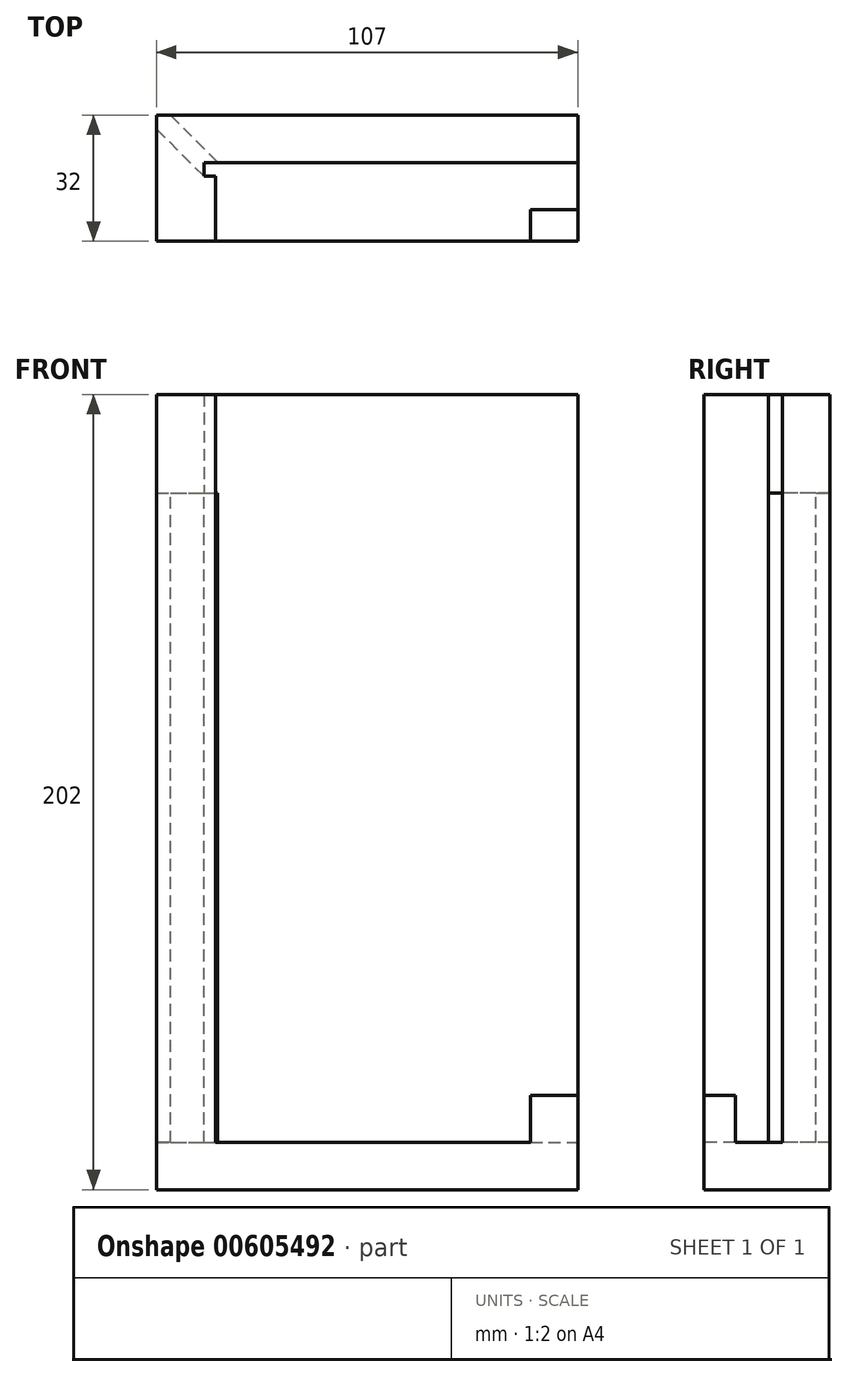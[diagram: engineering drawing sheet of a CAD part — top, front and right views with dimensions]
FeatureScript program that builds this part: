
annotation { "Feature Type Name" : "Feature", "Feature Type Description" : "" }
export const myFeature = defineFeature(function(context is Context, id is Id, definition is map)
    precondition{}
    {
        {
            var Q0;
            Q0=qCreatedBy(makeId("Top.planeOp"),FACE);
            var sketch = newSketch(context, id + "F0", { "sketchPlane" : qUnion([Q0])});
            skLineSegment(sketch, "E0", {"start": v(-28.32, 70.71) * mm, "end": v(-28.32, -10.33) * mm, "construction": true});
            skLineSegment(sketch, "E1", {"start": v(-27.64, -6.28) * mm, "end": v(-11.03, -22.9) * mm, "construction": true});
            skLineSegment(sketch, "E2", {"start": v(-15.41, -17.56) * mm, "end": v(106.8, -17.56) * mm, "construction": true});
            skLineSegment(sketch, "E3.0", {"start": v(-26.02, 70.71) * mm, "end": v(-26.02, -10.33) * mm, "construction": true});
            skLineSegment(sketch, "E4.0", {"start": v(-26.02, -4.66) * mm, "end": v(-9.4, -21.27) * mm, "construction": true});
            skLineSegment(sketch, "E5.0", {"start": v(-15.41, -15.26) * mm, "end": v(106.8, -15.26) * mm, "construction": true});
            skLineSegment(sketch, "E6.bottom", {"start": v(-15.41, -15.26) * mm, "end": v(79.59, -15.26) * mm});
            skLineSegment(sketch, "E6.top", {"start": v(-15.41, -3.26) * mm, "end": v(79.59, -3.26) * mm});
            skLineSegment(sketch, "E6.left", {"start": v(-15.41, -15.26) * mm, "end": v(-15.41, -3.26) * mm});
            skLineSegment(sketch, "E6.right", {"start": v(79.59, -15.26) * mm, "end": v(79.59, -3.26) * mm});
            skLineSegment(sketch, "E7.bottom", {"start": v(-15.41, -15.26) * mm, "end": v(-27.41, -15.26) * mm});
            skLineSegment(sketch, "E7.top", {"start": v(-15.41, -35.26) * mm, "end": v(-27.41, -35.26) * mm});
            skLineSegment(sketch, "E7.left", {"start": v(-15.41, -15.26) * mm, "end": v(-15.41, -35.26) * mm});
            skLineSegment(sketch, "E7.right", {"start": v(-27.41, -15.26) * mm, "end": v(-27.41, -35.26) * mm});
            skLineSegment(sketch, "E8.top", {"start": v(-15.41, -3.26) * mm, "end": v(-27.41, -3.26) * mm});
            skLineSegment(sketch, "E8.right", {"start": v(-27.41, -15.26) * mm, "end": v(-27.41, -3.26) * mm});
            skLineSegment(sketch, "E9", {"start": v(-27.41, -3.26) * mm, "end": v(-15.41, -15.26) * mm});
            skLineSegment(sketch, "E10.0", {"start": v(-27.79, -6.42) * mm, "end": v(-11.17, -23.04) * mm});
            skLineSegment(sketch, "E11.0", {"start": v(-23.88, -3.26) * mm, "end": v(-7.64, -19.5) * mm});
            skSolve(sketch);
        }
        {
            var Q0;
            {var subQ1=sQuery(id+"F0.wireOp",EDGE,"E6.top");Q0=makeQuery(id+"F0.imprint","IMPRINT",FACE,{"disambiguationData":[TD([[makeQuery(id+"F0.imprint","IMPRINT",EDGE,{"derivedFrom":subQ1}),-1.0]])]});}
            var Q1;
            {var subQ1=sQuery(id+"F0.wireOp",EDGE,"E8.top");var subQ3=sQuery(id+"F0.wireOp",EDGE,"E11.0");var subQ4=makeQuery(id+"F0.imprint","INTERSECT",VERTEX,{"derivedFrom":[subQ1,subQ3]});Q1=makeQuery(id+"F0.imprint","IMPRINT",FACE,{"disambiguationData":[TD([[makeQuery(id+"F0.imprint","IMPRINT",EDGE,{"disambiguationData":[TD([[subQ4,-1.0]])],"derivedFrom":subQ3}),1.0]])]});}
            var Q2;
            {var subQ0=sQuery(id+"F0.wireOp",EDGE,"E9");Q2=makeQuery(id+"F0.imprint","IMPRINT",FACE,{"disambiguationData":[TD([[makeQuery(id+"F0.imprint","IMPRINT",EDGE,{"derivedFrom":subQ0}),-1.0]])]});}
            var Q3;
            {var subQ0=sQuery(id+"F0.wireOp",EDGE,"E8.right");var subQ3=sQuery(id+"F0.wireOp",EDGE,"E10.0");var subQ5=makeQuery(id+"F0.imprint","INTERSECT",VERTEX,{"derivedFrom":[subQ0,subQ3]});Q3=makeQuery(id+"F0.imprint","IMPRINT",FACE,{"disambiguationData":[TD([[makeQuery(id+"F0.imprint","IMPRINT",EDGE,{"disambiguationData":[TD([[subQ5,-1.0]])],"derivedFrom":subQ3}),-1.0]])]});}
            var Q4;
            {var subQ6=sQuery(id+"F0.wireOp",EDGE,"E7.top");Q4=makeQuery(id+"F0.imprint","IMPRINT",FACE,{"disambiguationData":[TD([[makeQuery(id+"F0.imprint","IMPRINT",EDGE,{"derivedFrom":subQ6}),-1.0]])]});}
            var Q5;
            {var subQ0=sQuery(id+"F0.wireOp",EDGE,"E9");Q5=makeQuery(id+"F0.imprint","IMPRINT",FACE,{"disambiguationData":[TD([[makeQuery(id+"F0.imprint","IMPRINT",EDGE,{"derivedFrom":subQ0}),1.0]])]});}
            var Q6;
            {var subQ1=sQuery(id+"F0.wireOp",EDGE,"E6.bottom");var subQ3=sQuery(id+"F0.wireOp",EDGE,"E11.0");var subQ4=makeQuery(id+"F0.imprint","INTERSECT",VERTEX,{"derivedFrom":[subQ1,subQ3]});Q6=makeQuery(id+"F0.imprint","IMPRINT",FACE,{"disambiguationData":[TD([[makeQuery(id+"F0.imprint","IMPRINT",EDGE,{"disambiguationData":[TD([[subQ4,1.0]])],"derivedFrom":subQ3}),-1.0]])]});}
            var Q7;
            {var subQ1=sQuery(id+"F0.wireOp",EDGE,"E7.left");var subQ3=sQuery(id+"F0.wireOp",EDGE,"E10.0");var subQ4=makeQuery(id+"F0.imprint","INTERSECT",VERTEX,{"derivedFrom":[subQ1,subQ3]});Q7=makeQuery(id+"F0.imprint","IMPRINT",FACE,{"disambiguationData":[TD([[makeQuery(id+"F0.imprint","IMPRINT",EDGE,{"disambiguationData":[TD([[subQ4,1.0]])],"derivedFrom":subQ3}),1.0]])]});}
            extrude(context, id + "F1", {"entities" : qUnion([Q0, Q1, Q2, Q3, Q4, Q5, Q6, Q7]), "depth" : 25 * mm, "offsetDistance" : 25 * mm});
        }
        {
            var Q0;
            {var subQ6=sQuery(id+"F0.wireOp",EDGE,"E7.top");Q0=makeQuery(id+"F0.imprint","IMPRINT",FACE,{"disambiguationData":[TD([[makeQuery(id+"F0.imprint","IMPRINT",EDGE,{"derivedFrom":subQ6}),-1.0]])]});}
            var Q1;
            {var subQ1=sQuery(id+"F0.wireOp",EDGE,"E8.top");var subQ3=sQuery(id+"F0.wireOp",EDGE,"E11.0");var subQ4=makeQuery(id+"F0.imprint","INTERSECT",VERTEX,{"derivedFrom":[subQ1,subQ3]});Q1=makeQuery(id+"F0.imprint","IMPRINT",FACE,{"disambiguationData":[TD([[makeQuery(id+"F0.imprint","IMPRINT",EDGE,{"disambiguationData":[TD([[subQ4,-1.0]])],"derivedFrom":subQ3}),1.0]])]});}
            var Q2;
            {var subQ1=sQuery(id+"F0.wireOp",EDGE,"E6.top");Q2=makeQuery(id+"F0.imprint","IMPRINT",FACE,{"disambiguationData":[TD([[makeQuery(id+"F0.imprint","IMPRINT",EDGE,{"derivedFrom":subQ1}),-1.0]])]});}
            var Q3;
            {var subQ0=sQuery(id+"F0.wireOp",EDGE,"E8.right");var subQ3=sQuery(id+"F0.wireOp",EDGE,"E10.0");var subQ5=makeQuery(id+"F0.imprint","INTERSECT",VERTEX,{"derivedFrom":[subQ0,subQ3]});Q3=makeQuery(id+"F0.imprint","IMPRINT",FACE,{"disambiguationData":[TD([[makeQuery(id+"F0.imprint","IMPRINT",EDGE,{"disambiguationData":[TD([[subQ5,-1.0]])],"derivedFrom":subQ3}),-1.0]])]});}
            extrude(context, id + "F2", {"entities" : qUnion([Q0, Q1, Q2, Q3]), "operationType" : NewBodyOperationType.ADD, "oppositeDirection" : true, "depth" : 165 * mm, "offsetDistance" : 25 * mm});
        }
        {
            var Q0;
            Q0=makeQuery(id+"F2.opExtrude","CAP_FACE",FACE,{"disambiguationData":[OSD([sQuery(id+"F0.wireOp",EDGE,"E7.top"),sQuery(id+"F0.wireOp",EDGE,"E7.left"),sQuery(id+"F0.wireOp",EDGE,"E7.right"),sQuery(id+"F0.wireOp",EDGE,"E8.right"),sQuery(id+"F0.wireOp",EDGE,"E10.0")])],"isStart":false});
            var sketch = newSketch(context, id + "F3", { "sketchPlane" : qUnion([Q0])});
            skLineSegment(sketch, "E12.bottom", {"start": v(-15.41, 18.8) * mm, "end": v(-12.41, 18.8) * mm});
            skLineSegment(sketch, "E12.left", {"start": v(-15.41, 18.8) * mm, "end": v(-15.41, 30.8) * mm});
            skLineSegment(sketch, "E12.right", {"start": v(-12.41, 18.8) * mm, "end": v(-12.41, 30.8) * mm});
            skLineSegment(sketch, "E13.top", {"start": v(-12.41, 35.26) * mm, "end": v(-15.41, 35.26) * mm});
            skLineSegment(sketch, "E13.left", {"start": v(-12.41, 30.8) * mm, "end": v(-12.41, 35.26) * mm});
            skLineSegment(sketch, "E13.right", {"start": v(-15.41, 30.8) * mm, "end": v(-15.41, 35.26) * mm});
            skSolve(sketch);
        }
        {
            var Q0;
            Q0=qSketchRegion(id+"F3",true);
            var Q1;
            Q1=makeQuery(id+"F1.opExtrude","CAP_FACE",FACE,{"disambiguationData":[OSD([sQuery(id+"F0.wireOp",EDGE,"E6.bottom"),sQuery(id+"F0.wireOp",EDGE,"E6.top"),sQuery(id+"F0.wireOp",EDGE,"E6.right"),sQuery(id+"F0.wireOp",EDGE,"E7.top"),sQuery(id+"F0.wireOp",EDGE,"E7.left"),sQuery(id+"F0.wireOp",EDGE,"E7.right"),sQuery(id+"F0.wireOp",EDGE,"E8.top"),sQuery(id+"F0.wireOp",EDGE,"E8.right")])],"isStart":false});
            extrude(context, id + "F4", {"entities" : qUnion([Q0]), "operationType" : NewBodyOperationType.ADD, "endBound" : BoundingType.UP_TO_SURFACE, "oppositeDirection" : true, "depth" : 25 * mm, "endBoundEntityFace" : qUnion([Q1]), "offsetDistance" : 25 * mm});
        }
        {
            var Q0;
            Q0=makeQuery(id+"F2.opExtrude","CAP_FACE",FACE,{"disambiguationData":[OSD([sQuery(id+"F0.wireOp",EDGE,"E6.bottom"),sQuery(id+"F0.wireOp",EDGE,"E6.top"),sQuery(id+"F0.wireOp",EDGE,"E6.right"),sQuery(id+"F0.wireOp",EDGE,"E8.top"),sQuery(id+"F0.wireOp",EDGE,"E11.0")])],"isStart":false});
            var sketch = newSketch(context, id + "F5", { "sketchPlane" : qUnion([Q0])});
            skLineSegment(sketch, "E14.0.0", {"start": v(-12.41, 30.8) * mm, "end": v(-12.41, 35.26) * mm});
            skLineSegment(sketch, "E14.0.1", {"start": v(-12.41, 35.26) * mm, "end": v(-15.41, 35.26) * mm});
            skLineSegment(sketch, "E14.0.2", {"start": v(-15.41, 35.26) * mm, "end": v(-15.41, 30.8) * mm});
            skLineSegment(sketch, "E14.0.3", {"start": v(-15.41, 30.8) * mm, "end": v(-15.41, 18.8) * mm});
            skLineSegment(sketch, "E14.0.4", {"start": v(-15.41, 18.8) * mm, "end": v(-12.41, 18.8) * mm});
            skLineSegment(sketch, "E14.0.5", {"start": v(-12.41, 18.8) * mm, "end": v(-12.41, 30.8) * mm});
            skLineSegment(sketch, "E15.bottom", {"start": v(79.59, 15.26) * mm, "end": v(-12.41, 15.26) * mm});
            skLineSegment(sketch, "E15.top", {"start": v(79.59, 35.26) * mm, "end": v(-12.41, 35.26) * mm});
            skLineSegment(sketch, "E15.left", {"start": v(79.59, 15.26) * mm, "end": v(79.59, 35.26) * mm});
            skLineSegment(sketch, "E15.right", {"start": v(-12.41, 15.26) * mm, "end": v(-12.41, 35.26) * mm});
            skLineSegment(sketch, "E16.top", {"start": v(79.59, 27.26) * mm, "end": v(-12.41, 27.26) * mm});
            skLineSegment(sketch, "E16.left", {"start": v(79.59, 15.26) * mm, "end": v(79.59, 27.26) * mm});
            skLineSegment(sketch, "E16.right", {"start": v(-12.41, 15.26) * mm, "end": v(-12.41, 27.26) * mm});
            skLineSegment(sketch, "E17.bottom", {"start": v(79.59, 35.26) * mm, "end": v(67.59, 35.26) * mm});
            skLineSegment(sketch, "E17.top", {"start": v(79.59, 15.26) * mm, "end": v(67.59, 15.26) * mm});
            skLineSegment(sketch, "E17.left", {"start": v(79.59, 35.26) * mm, "end": v(79.59, 15.26) * mm});
            skLineSegment(sketch, "E17.right", {"start": v(67.59, 35.26) * mm, "end": v(67.59, 15.26) * mm});
            skSolve(sketch);
        }
        {
            var Q0;
            {var subQ0=sQuery(id+"F5.wireOp",EDGE,"E15.top");Q0=makeQuery(id+"F5.imprint","IMPRINT",FACE,{"disambiguationData":[TD([[makeQuery(id+"F5.imprint","IMPRINT",EDGE,{"derivedFrom":subQ0}),1.0]])]});}
            var Q1;
            {var subQ5=sQuery(id+"F5.wireOp",EDGE,"E17.bottom");Q1=makeQuery(id+"F5.imprint","IMPRINT",FACE,{"disambiguationData":[TD([[makeQuery(id+"F5.imprint","IMPRINT",EDGE,{"derivedFrom":subQ5}),1.0]])]});}
            var Q2;
            {var subQ5=sQuery(id+"F5.wireOp",EDGE,"E17.top");Q2=makeQuery(id+"F5.imprint","IMPRINT",FACE,{"disambiguationData":[TD([[makeQuery(id+"F5.imprint","IMPRINT",EDGE,{"derivedFrom":subQ5}),1.0]])]});}
            extrude(context, id + "F6", {"entities" : qUnion([Q0, Q1, Q2]), "operationType" : NewBodyOperationType.ADD, "oppositeDirection" : true, "depth" : 12 * mm, "offsetDistance" : 25 * mm});
        }
        {
            var Q0;
            Q0=makeQuery(id+"F6.boolean.opBoolean","MERGE",FACE,{"derivedFrom":[makeQuery(id+"F2.opExtrude","CAP_FACE",FACE,{"disambiguationData":[OSD([sQuery(id+"F0.wireOp",EDGE,"E6.bottom"),sQuery(id+"F0.wireOp",EDGE,"E6.top"),sQuery(id+"F0.wireOp",EDGE,"E6.right"),sQuery(id+"F0.wireOp",EDGE,"E8.top"),sQuery(id+"F0.wireOp",EDGE,"E11.0")])],"isStart":false}),makeQuery(id+"F4.boolean.opBoolean","MERGE",FACE,{"derivedFrom":[makeQuery(id+"F2.opExtrude","CAP_FACE",FACE,{"disambiguationData":[OSD([sQuery(id+"F0.wireOp",EDGE,"E7.top"),sQuery(id+"F0.wireOp",EDGE,"E7.left"),sQuery(id+"F0.wireOp",EDGE,"E7.right"),sQuery(id+"F0.wireOp",EDGE,"E8.right"),sQuery(id+"F0.wireOp",EDGE,"E10.0")])],"isStart":false}),makeQuery(id+"F4.opExtrude","CAP_FACE",FACE,{"disambiguationData":[OSD([sQuery(id+"F3.wireOp",EDGE,"E12.bottom"),sQuery(id+"F3.wireOp",EDGE,"E12.left"),sQuery(id+"F3.wireOp",EDGE,"E12.right"),sQuery(id+"F3.wireOp",EDGE,"E13.top"),sQuery(id+"F3.wireOp",EDGE,"E13.left"),sQuery(id+"F3.wireOp",EDGE,"E13.right")])],"isStart":true})]}),makeQuery(id+"F6.opExtrude","CAP_FACE",FACE,{"disambiguationData":[OSD([sQuery(id+"F5.wireOp",EDGE,"E15.top"),sQuery(id+"F5.wireOp",EDGE,"E15.right"),sQuery(id+"F5.wireOp",EDGE,"E16.top"),sQuery(id+"F5.wireOp",EDGE,"E17.bottom"),sQuery(id+"F5.wireOp",EDGE,"E17.top"),sQuery(id+"F5.wireOp",EDGE,"E17.left"),sQuery(id+"F5.wireOp",EDGE,"E17.right")])],"isStart":true})]});
            var sketch = newSketch(context, id + "F7", { "sketchPlane" : qUnion([Q0])});
            skLineSegment(sketch, "E18.bottom", {"start": v(79.59, 3.26) * mm, "end": v(-27.41, 3.26) * mm});
            skLineSegment(sketch, "E18.top", {"start": v(79.59, 35.26) * mm, "end": v(-27.41, 35.26) * mm});
            skLineSegment(sketch, "E18.left", {"start": v(79.59, 3.26) * mm, "end": v(79.59, 35.26) * mm});
            skLineSegment(sketch, "E18.right", {"start": v(-27.41, 3.26) * mm, "end": v(-27.41, 35.26) * mm});
            skSolve(sketch);
        }
        {
            var Q0;
            Q0 = qSketchRegion(id + "F7", true);
            extrude(context, id + "F8", {"entities" : qUnion([Q0]), "operationType" : NewBodyOperationType.ADD, "depth" : 12 * mm, "offsetDistance" : 25 * mm});
        }
    });
